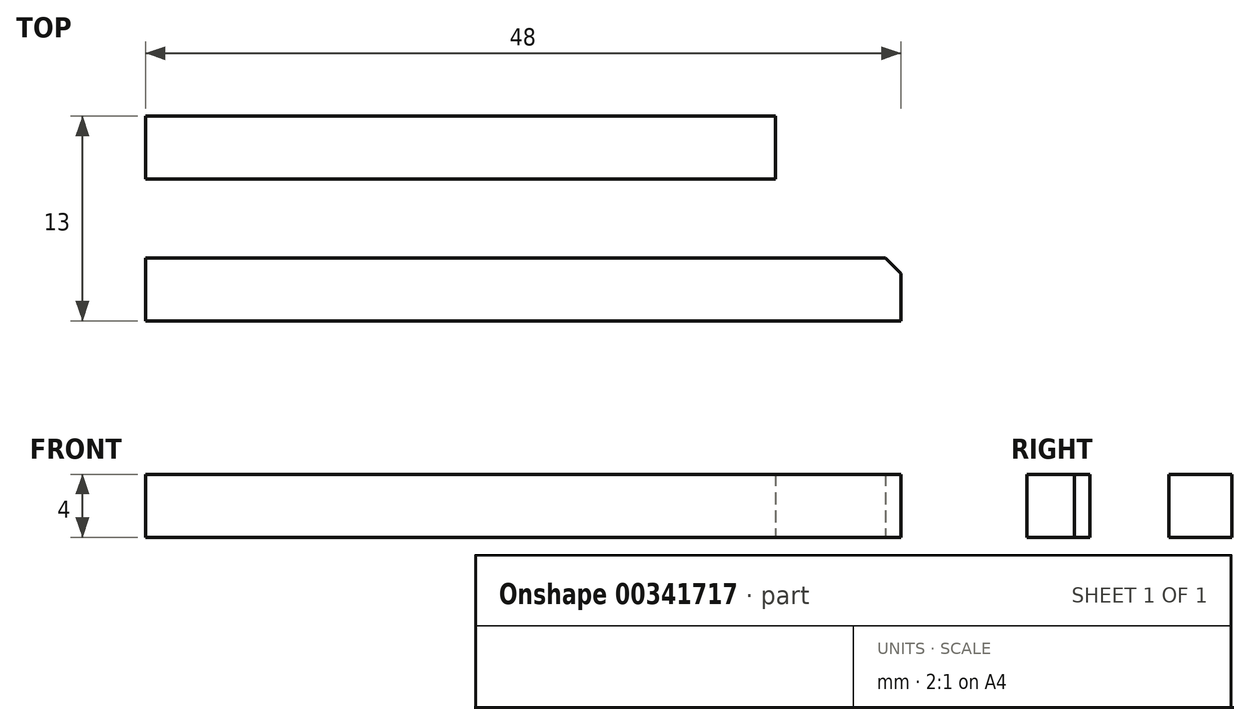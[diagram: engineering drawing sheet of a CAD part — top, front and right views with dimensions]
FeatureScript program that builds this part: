
annotation { "Feature Type Name" : "Feature", "Feature Type Description" : "" }
export const myFeature = defineFeature(function(context is Context, id is Id, definition is map)
    precondition{}
    {
        {
            var Q0;
            Q0=qCreatedBy(makeId("Top.planeOp"),FACE);
            var sketch = newSketch(context, id + "F0", { "sketchPlane" : qUnion([Q0])});
            skLineSegment(sketch, "E0.bottom", {"start": v(-19.79, 0) * mm, "end": v(20.21, 0) * mm});
            skLineSegment(sketch, "E0.top", {"start": v(-19.79, 4) * mm, "end": v(20.21, 4) * mm});
            skLineSegment(sketch, "E0.left", {"start": v(-19.79, 0) * mm, "end": v(-19.79, 4) * mm});
            skLineSegment(sketch, "E0.right", {"start": v(20.21, 0) * mm, "end": v(20.21, 4) * mm});
            skLineSegment(sketch, "E1.bottom", {"start": v(-19.79, 0) * mm, "end": v(-15.79, 0) * mm});
            skLineSegment(sketch, "E1.top", {"start": v(-19.79, -5) * mm, "end": v(-15.79, -5) * mm});
            skLineSegment(sketch, "E1.left", {"start": v(-19.79, 0) * mm, "end": v(-19.79, -5) * mm});
            skLineSegment(sketch, "E1.right", {"start": v(-15.79, 0) * mm, "end": v(-15.79, -5) * mm});
            skLineSegment(sketch, "E2.bottom", {"start": v(-19.79, -5) * mm, "end": v(28.21, -5) * mm});
            skLineSegment(sketch, "E2.top", {"start": v(-19.79, -9) * mm, "end": v(28.21, -9) * mm});
            skLineSegment(sketch, "E2.left", {"start": v(-19.79, -5) * mm, "end": v(-19.79, -9) * mm});
            skLineSegment(sketch, "E2.right", {"start": v(28.21, -5) * mm, "end": v(28.21, -9) * mm});
            skLineSegment(sketch, "E3.bottom", {"start": v(28.21, -5) * mm, "end": v(24.21, -5) * mm});
            skLineSegment(sketch, "E3.top", {"start": v(28.21, 0.97) * mm, "end": v(24.21, 0.97) * mm});
            skLineSegment(sketch, "E3.left", {"start": v(28.21, -5) * mm, "end": v(28.21, 0.97) * mm});
            skLineSegment(sketch, "E3.right", {"start": v(24.21, -5) * mm, "end": v(24.21, 0.97) * mm});
            skSolve(sketch);
        }
        {
            var Q0;
            Q0=makeQuery(id+"F0.imprint","IMPRINT",FACE,{"disambiguationData":[TD([[makeQuery(id+"F0.imprint","IMPRINT",EDGE,{"derivedFrom":sQuery(id+"F0.wireOp",EDGE,"E3.bottom")}),-1.0]])]});
            var Q1;
            Q1=makeQuery(id+"F0.imprint","IMPRINT",FACE,{"disambiguationData":[TD([[makeQuery(id+"F0.imprint","IMPRINT",EDGE,{"derivedFrom":sQuery(id+"F0.wireOp",EDGE,"E0.bottom")}),1.0]])]});
            var Q2;
            Q2=makeQuery(id+"F0.imprint","IMPRINT",FACE,{"disambiguationData":[TD([[makeQuery(id+"F0.imprint","IMPRINT",EDGE,{"derivedFrom":sQuery(id+"F0.wireOp",EDGE,"E1.bottom")}),-1.0]])]});
            var Q3;
            Q3=makeQuery(id+"F0.imprint","IMPRINT",FACE,{"disambiguationData":[TD([[makeQuery(id+"F0.imprint","IMPRINT",EDGE,{"derivedFrom":sQuery(id+"F0.wireOp",EDGE,"E2.top")}),1.0]])]});
            extrude(context, id + "F1", {"entities" : qUnion([Q0, Q1, Q2, Q3]), "depth" : 4 * mm});
        }
        {
            var Q0;
            Q0=makeQuery(id+"F1.opExtrude","SWEPT_EDGE",EDGE,{"disambiguationData":[OSD([sQuery(id+"F0.wireOp",EDGE,"E3.top"),sQuery(id+"F0.wireOp",EDGE,"E3.right")])]});
            var Q1;
            Q1=makeQuery(id+"F1.opExtrude","SWEPT_EDGE",EDGE,{"disambiguationData":[OSD([sQuery(id+"F0.wireOp",EDGE,"E3.top"),sQuery(id+"F0.wireOp",EDGE,"E3.left")])]});
            chamfer(context, id + "F2", {"entities" : qUnion([Q0, Q1]), "width" : 1 * mm, "tangentPropagation" : true});
        }
    });
